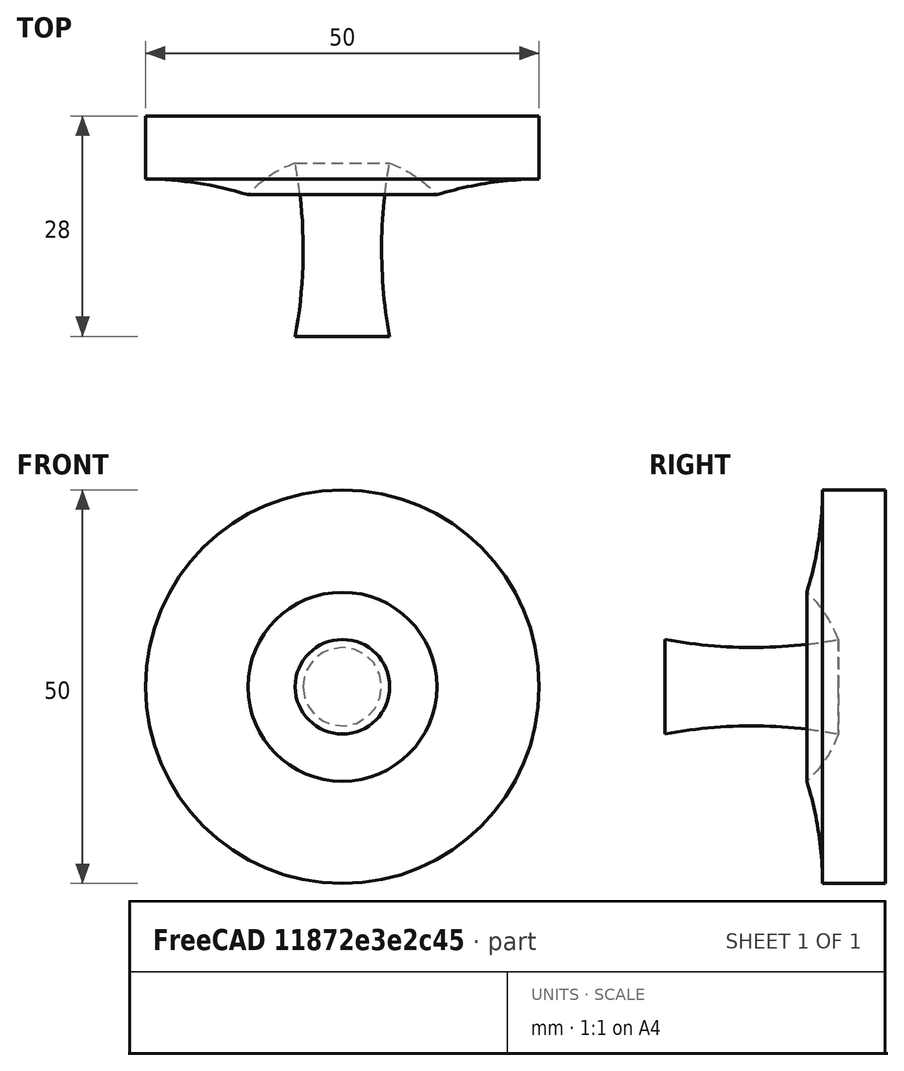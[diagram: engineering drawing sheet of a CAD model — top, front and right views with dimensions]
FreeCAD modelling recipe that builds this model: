
FCSTD DOCUMENT  (FreeCAD 0.20R29410 (Git))
Label: MangoJelly_Solutions_Tutorial_Ep8
License: All rights reserved
LicenseURL: http://en.wikipedia.org/wiki/All_rights_reserved
objects: Sketcher::SketchObject×1, PartDesign::Revolution×1, PartDesign::Body×1
note: 4 computed .brp shape members not serialized (recipe doc carries the construction recipe); baked Part::Feature solids carry a one-line shape summary decoded from their .brp

FEATURE [Sketcher::SketchObject] Sketch
  FullyConstrained = true
  sketch-geometry (13):
    g0: GeomPoint X=-25 Y=10 Z=0
    g1: GeomPoint X=-6 Y=12 Z=0
    g2: GeomPoint X=-6 Y=-10 Z=0
    g3: GeomPoint X=-25 Y=18 Z=0
    g4: GeomPoint X=-12 Y=8 Z=0
    g5: GeomPoint X=0 Y=22 Z=0
    g6: LineSegment StartX=-25 StartY=18 StartZ=0 EndX=-25 EndY=10 EndZ=0
    g7: ArcOfCircle CenterX=-25.2691 CenterY=-34.9992 CenterZ=0 NormalX=0 NormalY=0 NormalZ=1 AngleXU=0 Radius=45 StartAngle=1.27148 EndAngle=1.56482
    g8: ArcOfCircle CenterX=-0.923443 CenterY=-2.11484 CenterZ=0 NormalX=0 NormalY=0 NormalZ=1 AngleXU=0 Radius=15 StartAngle=1.91605 EndAngle=2.40155
    g9: LineSegment StartX=-6 StartY=-10 StartZ=0 EndX=0 EndY=-10 EndZ=0
    g10: ArcOfCircle CenterX=-23.377 CenterY=87.9812 CenterZ=0 NormalX=0 NormalY=0 NormalZ=1 AngleXU=0 Radius=70 StartAngle=4.6892 EndAngle=5.05289
    g11: ArcOfCircle CenterX=-64.983 CenterY=1 CenterZ=0 NormalX=0 NormalY=0 NormalZ=1 AngleXU=0 Radius=60 StartAngle=6.09881 EndAngle=6.46756
    g12: LineSegment StartX=0 StartY=-10 StartZ=0 EndX=0 EndY=22 EndZ=0
  constraints (31):
    c: Vertical(g1,g2)
    c: DistanceX(g1,g-1) = 6
    c: Vertical(g3,g0)
    c: DistanceY(g0,g3) = 8
    c: DistanceX(g0,g-1) = 25
    c: DistanceX(g4,g-1) = 12
    c: DistanceY(g4,g0) = 2
    c: DistanceY(g-1,g1) = 12
    c: DistanceY(g2,g4) = 18
    c: Coincident(g6,g3)
    c: Coincident(g6,g0)
    c: Coincident(g7,g0)
    c: Coincident(g7,g4)
    c: Coincident(g8,g4)
    c: Coincident(g8,g1)
    c: Coincident(g9,g2)
    c: Horizontal(g9)
    c: Coincident(g10,g3)
    c: Coincident(g11,g1)
    c: Coincident(g11,g2)
    c: Coincident(g10,g5)
    c: PointOnObject(g10,g-2)
    c: DistanceY(g4,g10) = 14
    c: PointOnObject(g9,g-2)
    c: DistanceY(g2,g-1) = 10
    c: Radius(g10) = 70
    c: Radius(g7) = 45
    c: Radius(g8) = 15
    c: Radius(g11) = 60
    c: Coincident(g12,g9)
    c: Coincident(g12,g10)
FEATURE [PartDesign::Revolution] Revolution
  Angle = 360
  Axis = (0,1,0)
  Base = (0,0,0)
  Profile = -> Sketch
  ReferenceAxis = -> Sketch [V_Axis]
FEATURE [PartDesign::Body] Body
  Group = -> [Sketch,Revolution]
  Origin = -> Origin
  Tip = -> Revolution
